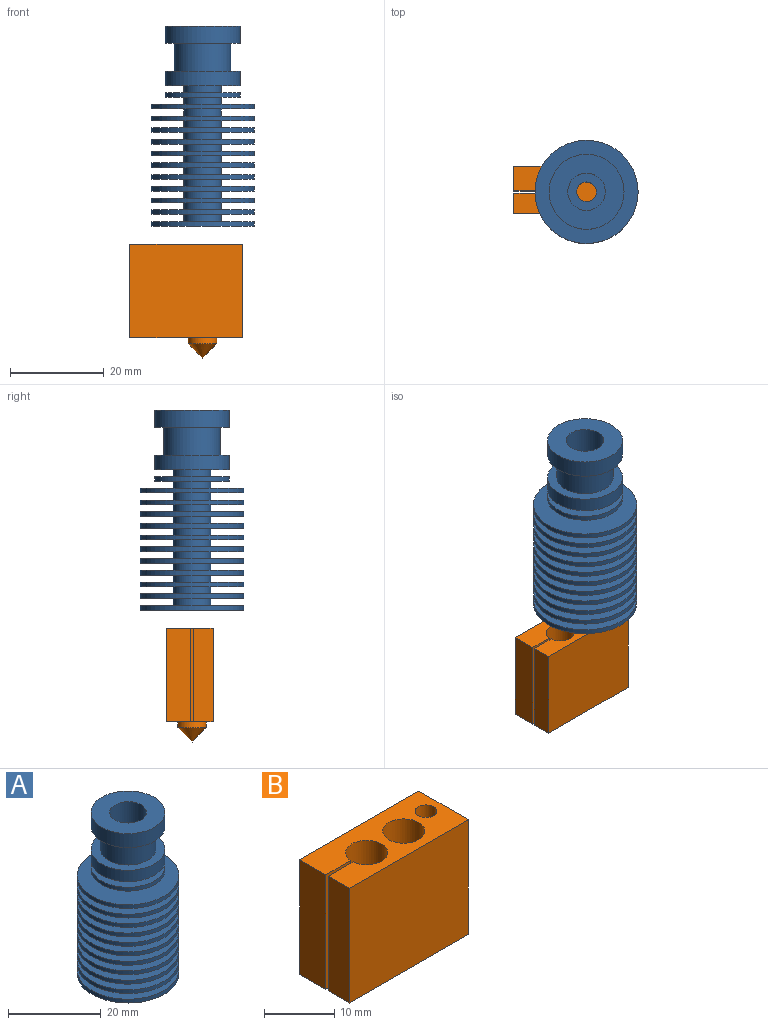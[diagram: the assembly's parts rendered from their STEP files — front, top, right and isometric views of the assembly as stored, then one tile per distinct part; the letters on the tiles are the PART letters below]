
ASSEMBLY  parts=2 mates=1
PART A: 60 faces, bbox 22x22x42.7 mm
  f0: cylinder r=4mm len=8mm, axis (0,0,1), area 163.4mm2, adj f1,f59
  f1: plane 16x16mm, normal (0,0,1), area 150.8mm2, adj f0,f2
  f2: cylinder r=8mm len=16mm, axis (0,0,1), area 186mm2, adj f1,f3
  f3: plane 16x16mm, normal (0,0,-1), area 88mm2, adj f2,f4
  f4: cylinder r=6mm len=12mm, axis (0,0,1), area 226.2mm2, adj f3,f5
  f5: plane 16x16mm, normal (0,0,1), area 88mm2, adj f4,f6
  f6: cylinder r=8mm len=16mm, axis (0,0,1), area 150.8mm2, adj f5,f7
  f7: plane 16x16mm, normal (0,0,-1), area 150.8mm2, adj f6,f8
  f8: cylinder r=4mm len=8mm, axis (0,0,1), area 37.7mm2, adj f7,f9
  f9: plane 16x16mm, normal (0,0,1), area 150.8mm2, adj f8,f10
  f10: cylinder r=8mm len=16mm, axis (0,0,1), area 50.3mm2, adj f9,f11
  f11: plane 16x16mm, normal (0,0,-1), area 150.8mm2, adj f10,f12
  f12: cylinder r=4mm len=8mm, axis (0,0,1), area 37.7mm2, adj f11,f13
  f13: plane 22x22mm, normal (0,0,1), area 329.9mm2, adj f12,f14
  f14: cylinder r=11mm len=22mm, axis (0,0,1), area 69.1mm2, adj f13,f15
  f15: plane 22x22mm, normal (0,0,-1), area 329.9mm2, adj f14,f16
  f16: cylinder r=4mm len=8mm, axis (0,0,1), area 37.7mm2, adj f15,f17
  f17: plane 22x22mm, normal (0,0,1), area 329.9mm2, adj f16,f18
  f18: cylinder r=11mm len=22mm, axis (0,0,1), area 69.1mm2, adj f17,f19
  f19: plane 22x22mm, normal (0,0,-1), area 329.9mm2, adj f18,f20
  f20: cylinder r=4mm len=8mm, axis (0,0,1), area 37.7mm2, adj f19,f21
  f21: plane 22x22mm, normal (0,0,1), area 329.9mm2, adj f20,f22
  f22: cylinder r=11mm len=22mm, axis (0,0,1), area 69.1mm2, adj f21,f23
  f23: plane 22x22mm, normal (0,0,-1), area 329.9mm2, adj f22,f24
  f24: cylinder r=4mm len=8mm, axis (0,0,1), area 37.7mm2, adj f23,f25
  f25: plane 22x22mm, normal (0,0,1), area 329.9mm2, adj f24,f26
  f26: cylinder r=11mm len=22mm, axis (0,0,1), area 69.1mm2, adj f25,f27
  f27: plane 22x22mm, normal (0,0,-1), area 329.9mm2, adj f26,f28
  f28: cylinder r=4mm len=8mm, axis (0,0,1), area 37.7mm2, adj f27,f29
  f29: plane 22x22mm, normal (0,0,1), area 329.9mm2, adj f28,f30
  f30: cylinder r=11mm len=22mm, axis (0,0,1), area 69.1mm2, adj f29,f31
  f31: plane 22x22mm, normal (0,0,-1), area 329.9mm2, adj f30,f32
  f32: cylinder r=4mm len=8mm, axis (0,0,1), area 37.7mm2, adj f31,f33
  f33: plane 22x22mm, normal (0,0,1), area 329.9mm2, adj f32,f34
  f34: cylinder r=11mm len=22mm, axis (0,0,1), area 69.1mm2, adj f33,f35
  f35: plane 22x22mm, normal (0,0,-1), area 329.9mm2, adj f34,f36
  f36: cylinder r=4mm len=8mm, axis (0,0,1), area 37.7mm2, adj f35,f37
  f37: plane 22x22mm, normal (0,0,1), area 329.9mm2, adj f36,f38
  f38: cylinder r=11mm len=22mm, axis (0,0,1), area 69.1mm2, adj f37,f39
  f39: plane 22x22mm, normal (0,0,-1), area 329.9mm2, adj f38,f40
  f40: cylinder r=4mm len=8mm, axis (0,0,1), area 37.7mm2, adj f39,f41
  f41: plane 22x22mm, normal (0,0,1), area 329.9mm2, adj f40,f42
  f42: cylinder r=11mm len=22mm, axis (0,0,1), area 69.1mm2, adj f41,f43
  f43: plane 22x22mm, normal (0,0,-1), area 329.9mm2, adj f42,f44
  f44: cylinder r=4mm len=8mm, axis (0,0,1), area 37.7mm2, adj f43,f45
  f45: plane 22x22mm, normal (0,0,1), area 329.9mm2, adj f44,f46
  f46: cylinder r=11mm len=22mm, axis (0,0,1), area 69.1mm2, adj f45,f47
  f47: plane 22x22mm, normal (0,0,-1), area 329.9mm2, adj f46,f48
  f48: cylinder r=4mm len=8mm, axis (0,0,1), area 37.7mm2, adj f47,f49
  f49: plane 22x22mm, normal (0,0,1), area 329.9mm2, adj f48,f50
  f50: cylinder r=11mm len=22mm, axis (0,0,1), area 69.1mm2, adj f49,f51
  f51: plane 22x22mm, normal (0,0,-1), area 329.9mm2, adj f50,f52
  f52: cylinder r=4mm len=8mm, axis (0,0,1), area 37.7mm2, adj f51,f53
  f53: plane 22x22mm, normal (0,0,1), area 329.9mm2, adj f52,f54
  f54: cylinder r=11mm len=22mm, axis (0,0,1), area 69.1mm2, adj f53,f55
  f55: plane 22x22mm, normal (0,0,-1), area 351.9mm2, adj f54,f56
  f56: cylinder r=3mm len=15.1mm, axis (0,0,1), area 284.6mm2, adj f55,f57
  f57: plane 6x6mm, normal (0,0,-1), area 14.4mm2, adj f56,f58
  f58: cylinder r=2.1mm len=21.1mm, axis (0,0,1), area 278.4mm2, adj f57,f59
  f59: plane 8x8mm, normal (0,0,1), area 36.4mm2, adj f0,f58
PART B: 15 faces, bbox 24x10x24.3 mm
  f0: plane 20x4.25mm, normal (-1,0,0), area 85mm2, adj f2,f3,f5,f14
  f1: cylinder r=3mm len=20mm, axis (0,0,-1), area 367mm2, adj f2,f3,f13,f14
  f2: plane 24x10mm, normal (0,0,1), area 173.4mm2, adj f0,f1,f4,f5,f6,f7,f8,f9
  f3: plane 24x10mm, normal (0,0,-1), area 172.4mm2, adj f0,f1,f4,f5,f6,f8,f9,f11
  f4: plane 20x5.25mm, normal (-1,0,0), area 105mm2, adj f2,f3,f9,f13
  f5: plane 24x20mm, normal (0,-1,0), area 480mm2, adj f0,f2,f3,f6
  f6: plane 20x10mm, normal (1,0,0), area 200mm2, adj f2,f3,f5,f9
  f7: cylinder r=3mm len=20mm, axis (0,0,-1), area 377mm2, adj f2,f12
  f8: cylinder r=1.55mm len=20mm, axis (0,0,-1), area 194.8mm2, adj f2,f3
  f9: plane 24x20mm, normal (0,1,0), area 480mm2, adj f2,f3,f4,f6
  f10: cone r=3.05mm half-angle=44.8deg, axis (0,0,1), area 41.5mm2, adj f11
  f11: cylinder r=3.05mm len=6.1mm, axis (0,0,-1), area 23.8mm2, adj f3,f10
  f12: plane 6x6mm, normal (0,0,1), area 28.3mm2, adj f7
  f13: plane 20x5.01mm, normal (0,-1,0), area 100.2mm2, adj f1,f2,f3,f4
  f14: plane 20x5.01mm, normal (0,1,0), area 100.2mm2, adj f0,f1,f2,f3
PLACE A at identity
PLACE B t=(-15.5,0,-56.5)mm
MATE planar B.f3 <-> A.f0  axis (0,0,-1) through (-12.99,-0.25,-66.5)mm
